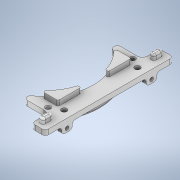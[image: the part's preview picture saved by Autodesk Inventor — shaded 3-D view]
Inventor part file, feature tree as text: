
AUTODESK INVENTOR PART (.ipt)
format: ipt  version: 2022 (Build 260153000, 153)  size: 4,648,960 bytes
history: native  units: in
note: dims shown in document units (in); Inventor stores cm internally (conversion verified against a paired STEP export)
features: sketch x14, extrude x9, fillet x9, hole x3, mirror x2, chamfer x2, plane x1, sweep x1
ambient origin geometry x8: Origin, YZ Plane, XZ Plane, XY Plane, X Axis, Y Axis, Z Axis, Center Point
bodies: Solid1 (feature_tree)
feature tree (41):
  extrude  "Extrusion1"  Depth=2.811in
  extrude  "Extrusion2"  Depth=0.1181in
  hole  "Hole1"  [1 undecoded]
  extrude  "Extrusion3"  Depth=0.1181in
  fillet  "Fillet1"  Radius=0.1181in
  fillet  "Fillet2"  Radius=0.376in
  fillet  "Fillet6"  Radius=0.1181in
  plane  "Work Plane1"
  mirror  "Mirror1"
  extrude  "Extrusion9"  Depth=0.1181in TaperAngle=0.0deg
  sweep  "Sweep5"
  extrude  "Extrusion10"  Depth=0.1181in
  extrude  "Extrusion11"  Depth=0.1181in
  fillet  "Fillet11"  Radius=0.1181in
  mirror  "Mirror2"
  fillet  "Fillet12"  Radius=2.2677in
  hole  "Hole4"  [1 undecoded]
  chamfer  "Chamfer3"  Distance=1.4055in
  extrude  "Extrusion12"  Depth=0.0394in
  fillet  "Fillet13"  Radius=2.5433in
  fillet  "Fillet14"  Radius=1.5748in
  hole  "Hole5"  [1 undecoded]
  chamfer  "Chamfer4"  Distance=0.3022in
  extrude  "Extrusion13"  Depth=0.0394in
  fillet  "Fillet15"  Radius=0.0992in
  extrude  "Extrusion14"  Depth=0.0394in TaperAngle=0.0deg
  fillet  "Fillet16"  Radius=0.0394in
  sketch  "Sketch1"  dims[d0=0.315in d1=2.811in]
  sketch  "Sketch2"  dims[d2=0.1181in d3=0.0in d7=0.1181in]
  sketch  "Sketch3"  dims[d8=0.1181in d9=0.1102in]
  sketch  "Sketch4"  dims[d10=0.0669in d13=1.4055in d14=0.1181in d15=0.376in d16=0.1181in]
  sketch  "Sketch15"  dims[d17=0.7874in d19=360.0deg d21=0.1181in d22=0.0in]
  sketch  "Sketch17"  dims[d23=0.124in d24=0.2362in d25=0.1575in d26=0.0787in d27=90.0deg d28=0.315in d29=0.8108in d30=0.1181in]
  sketch  "3D Sketch4"
  sketch  "Sketch18"  dims[d31=0.378in d32=0.1181in]
  sketch  "Sketch19"  dims[d33=0.378in d34=0.1181in d35=0.1181in d38=2.2677in]
  sketch  "Sketch20"  dims[d39=180.0deg d41=0.1181in d42=0.0in]
  sketch  "Sketch21"  dims[d43=0.0787in]
  sketch  "Sketch22"  dims[d52=0.1181in]
  sketch  "Sketch23"  dims[d81=0.0394in]
  sketch  "Sketch25"  dims[d126=1.1811in d127=1.4055in d128=2.1654in d134=2.5433in d135=1.5748in d137=0.3022in d138=0.3022in d139=0.0992in d140=0.0992in d141=0.2953in d142=0.0in d151=0.0394in d152=0.2008in d153=0.0374in d154=0.0in d155=0.0in d157=0.2165in d158=0.2165in d159=0.1575in d160=0.0in d161=0.0787in d162=0.1969in d163=0.0in d164=0.0in d165=0.0787in d166=0.0394in d167=0.1018in d168=0.437in d169=0.437in d171=0.1018in d172=0.0866in d173=0.2362in d174=0.1575in d175=0.0787in d176=90.0deg d177=0.315in d178=0.8108in d179=0.0197in d180=0.0787in d181=45.0deg d182=0.2441in d183=0.3813in d188=0.1348in d189=0.0in d194=0.1654in d195=0.0in d196=0.0709in d197=0.2441in d198=0.3813in d199=0.1348in d200=0.0709in d201=0.0512in d202=0.0827in d203=0.0512in d204=0.0827in d205=0.0866in d206=0.2362in d207=0.1575in d208=0.0787in d209=90.0deg d210=0.315in d211=0.8108in d212=0.0197in d213=0.0787in d214=45.0deg d215=0.1831in d216=0.1831in d217=0.1654in d218=0.0in d219=0.0197in d220=0.4134in d221=0.5906in d222=0.2323in d223=0.3386in d224=0.1181in d225=0.0in d227=0.0394in]
note: 3 required parameter values undecoded (feature->parameter linkage not recoverable at this tier; creation-order binding heuristic only, values carry confidence <= 0.55)
